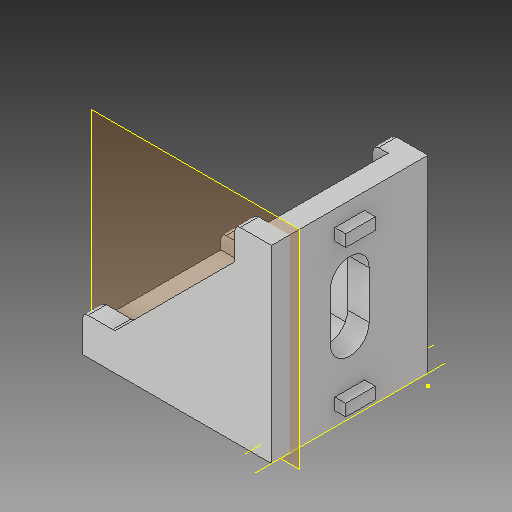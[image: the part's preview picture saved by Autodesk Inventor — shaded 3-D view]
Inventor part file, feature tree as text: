
AUTODESK INVENTOR PART (.ipt)
format: ipt  version: 2017 (Build 210142000, 142)  size: 179,200 bytes
history: native  units: mm
features: sketch x7, other x5, plane x1
ambient origin geometry x8: Origin, YZ Plane, XZ Plane, XY Plane, X Axis, Y Axis, Z Axis, Center Point
bodies: Solid1 (feature_tree)
feature tree (13):
  other  "30mm Bracket_MIR2.ipt"
  other  "Solid1::30mm Bracket_MIR2.ipt"
  other  "TaggingFeature1"
  sketch  "Sketch1"  dims[d0=10.0mm]
  sketch  "Sketch2"
  sketch  "Sketch3"
  sketch  "Sketch4"
  sketch  "Sketch5"
  sketch  "Sketch7"
  sketch  "Sketch9"
  plane  "Work Plane1"
  other  "Work Axis1"
  other  "Work Axis2"
